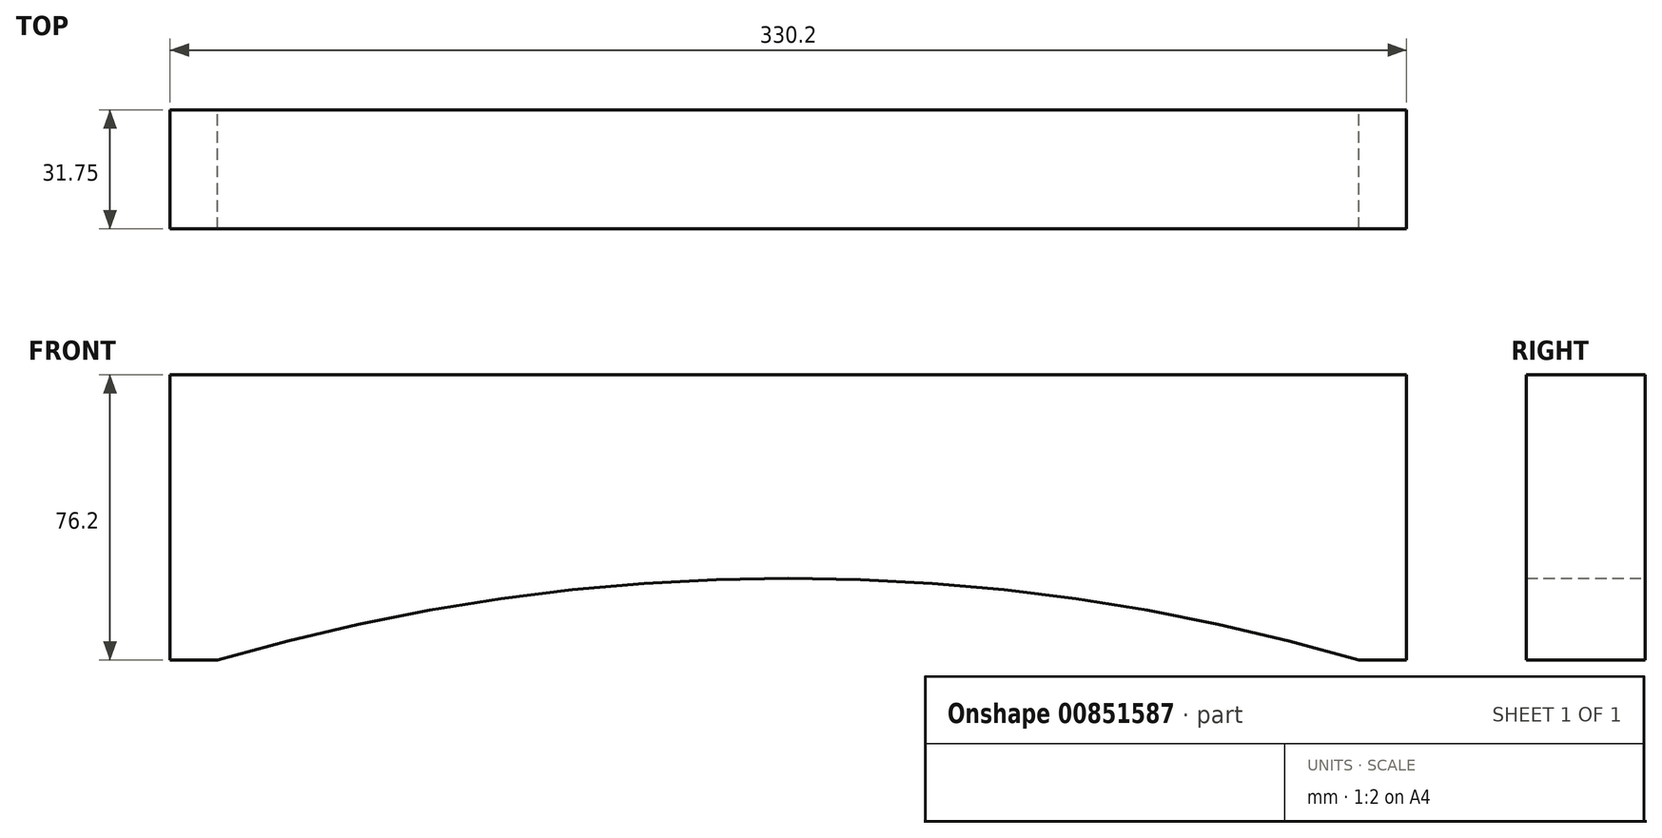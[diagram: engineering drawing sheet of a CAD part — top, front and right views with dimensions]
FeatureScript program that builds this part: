
annotation { "Feature Type Name" : "Feature", "Feature Type Description" : "" }
export const myFeature = defineFeature(function(context is Context, id is Id, definition is map)
    precondition{}
    {
        {
            var Q0;
            Q0=qCreatedBy(makeId("Front.planeOp"),FACE);
            var sketch = newSketch(context, id + "F0", { "sketchPlane" : qUnion([Q0])});
            skLineSegment(sketch, "E0", {"start": v(94.48, 25.21) * mm, "end": v(-235.72, 25.21) * mm});
            skLineSegment(sketch, "E1", {"start": v(-235.72, 25.21) * mm, "end": v(-235.72, -50.99) * mm});
            skLineSegment(sketch, "E2", {"start": v(-235.72, -50.99) * mm, "end": v(-223.02, -50.99) * mm});
            skLineSegment(sketch, "E3", {"start": v(94.48, 25.21) * mm, "end": v(94.48, -50.99) * mm});
            skLineSegment(sketch, "E4", {"start": v(94.48, -50.99) * mm, "end": v(81.78, -50.99) * mm});
            skArc(sketch, "E5", {"start": v(81.78, -50.99) * mm, "mid": v(-70.62, -29.14) * mm, "end": v(-223.02, -50.99) * mm});
            skSolve(sketch);
        }
        {
            var Q0;
            Q0=qSketchRegion(id+"F0",true);
            extrude(context, id + "F1", {"entities" : qUnion([Q0]), "depth" : 31.75 * mm, "offsetDistance" : 25.4 * mm});
        }
    });
